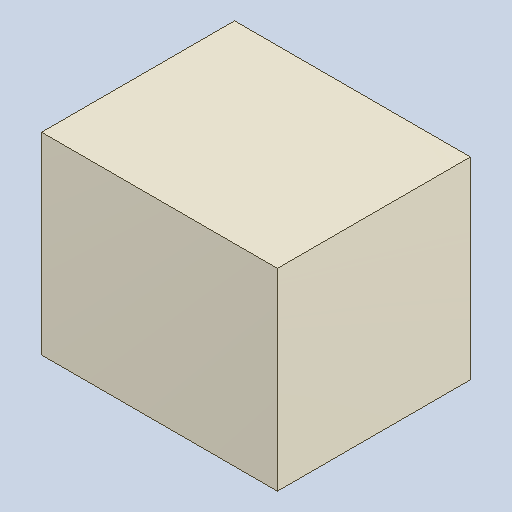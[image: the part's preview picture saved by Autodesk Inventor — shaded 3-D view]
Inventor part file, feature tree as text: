
AUTODESK INVENTOR PART (.ipt)
format: ipt  version: 2023.4 (Build 274418000, 418)  size: 81,920 bytes
history: native  units: mm
features: extrude x1
ambient origin geometry x8: Origin, YZ Plane, XZ Plane, XY Plane, X Axis, Y Axis, Z Axis, Center Point
bodies: Solid1 (feature_tree)
feature tree (1):
  extrude  "Extruded_19"  [1 undecoded]
note: 1 required parameter value undecoded (feature->parameter linkage not recoverable at this tier; creation-order binding heuristic only, values carry confidence <= 0.55)
